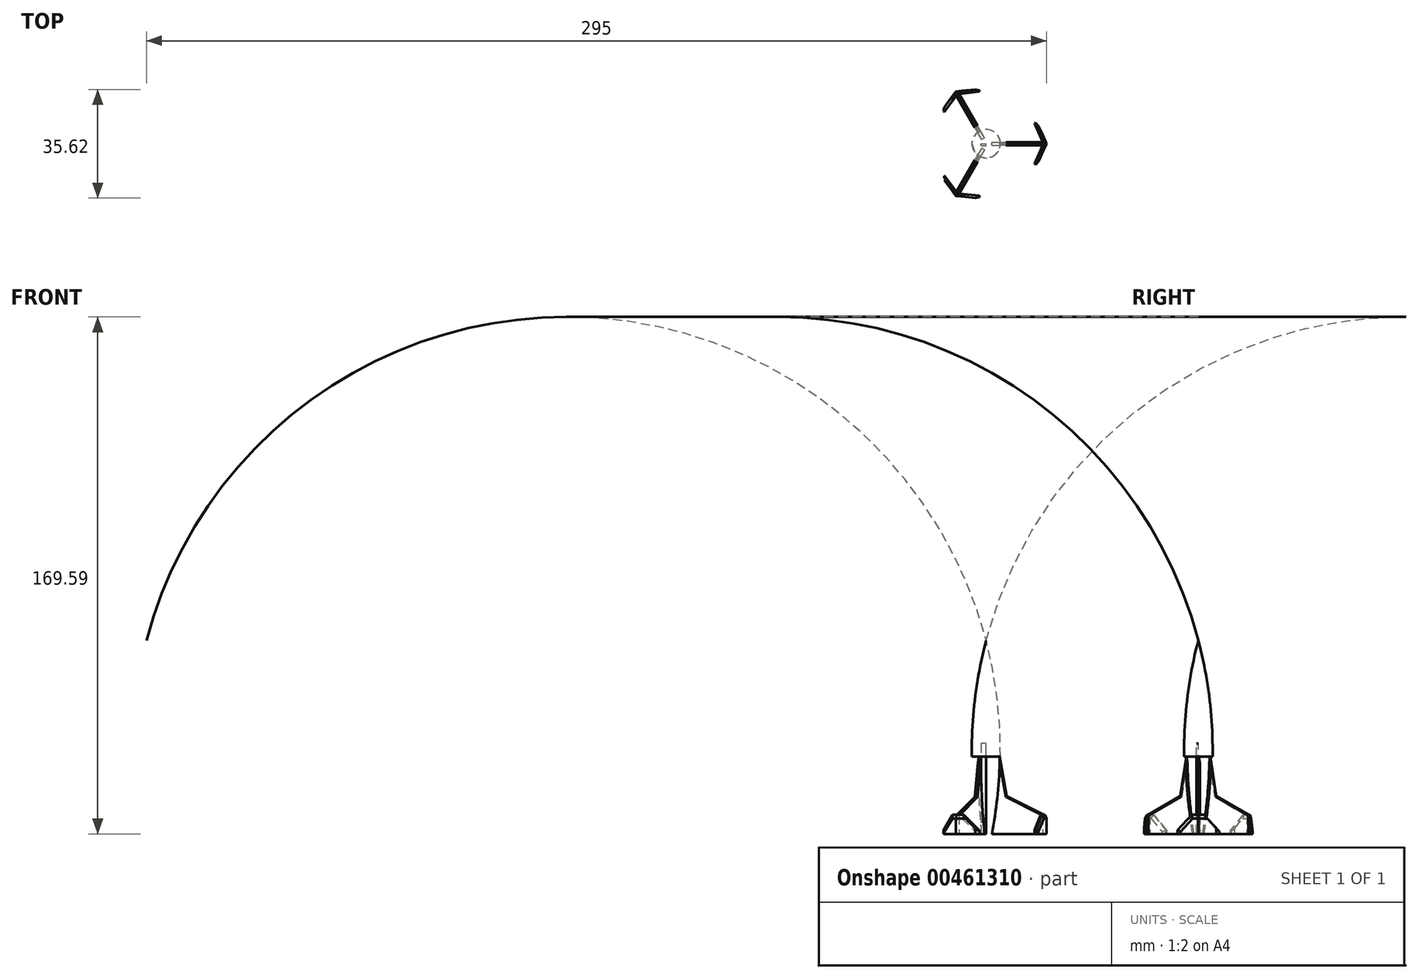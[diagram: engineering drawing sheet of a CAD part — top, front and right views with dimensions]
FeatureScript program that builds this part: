
annotation { "Feature Type Name" : "Feature", "Feature Type Description" : "" }
export const myFeature = defineFeature(function(context is Context, id is Id, definition is map)
    precondition{}
    {
        {
            var Q0;
            Q0=qCreatedBy(makeId("Front.planeOp"),FACE);
            var sketch = newSketch(context, id + "F0", { "sketchPlane" : qUnion([Q0])});
            skLineSegment(sketch, "E0", {"start": v(0, 0) * mm, "end": v(0, 63.5) * mm});
            skLineSegment(sketch, "E1", {"start": v(0, 0) * mm, "end": v(0, 25.4) * mm});
            skLineSegment(sketch, "E2", {"start": v(0, 25.4) * mm, "end": v(4.67, 25.4) * mm});
            skLineSegment(sketch, "E3", {"start": v(0, 0) * mm, "end": v(3.18, 0) * mm});
            skLineSegment(sketch, "E4", {"start": v(0, 0) * mm, "end": v(19.05, 0) * mm});
            skLineSegment(sketch, "E5", {"start": v(19.05, 0) * mm, "end": v(19.05, 6.35) * mm});
            skLineSegment(sketch, "E6", {"start": v(6.93, 12.46) * mm, "end": v(19.05, 6.35) * mm});
            skLineSegment(sketch, "E7", {"start": v(0, 0) * mm, "end": v(2.04, 0) * mm});
            skLineSegment(sketch, "E8", {"start": v(0, 0) * mm, "end": v(0, 19.05) * mm});
            skLineSegment(sketch, "E9", {"start": v(0, 19.05) * mm, "end": v(4.45, 19.05) * mm});
            skArc(sketch, "E10", {"start": v(2.04, 0) * mm, "mid": v(4.61, 31.87) * mm, "end": v(0, 63.5) * mm});
            skLineSegment(sketch, "E11", {"start": v(4.67, 25.4) * mm, "end": v(6.93, 12.46) * mm});
            skSolve(sketch);
        }
        {
            var Q0;
            {var subQ0=sQuery(id+"F0.wireOp",EDGE,"E0");Q0=makeQuery(id+"F0.imprint","IMPRINT",FACE,{"disambiguationData":[TD([[makeQuery(id+"F0.imprint","IMPRINT",EDGE,{"derivedFrom":subQ0}),-1.0]])]});}
            var Q1;
            {var subQ0=sQuery(id+"F0.wireOp",EDGE,"E1");Q1=makeQuery(id+"F0.imprint","IMPRINT",FACE,{"disambiguationData":[TD([[makeQuery(id+"F0.imprint","IMPRINT",EDGE,{"derivedFrom":subQ0}),-1.0]])]});}
            var Q2;
            Q2=makeQuery(id+"F0.imprint","IMPRINT",FACE,{"disambiguationData":[TD([[makeQuery(id+"F0.imprint","IMPRINT",EDGE,{"derivedFrom":sQuery(id+"F0.wireOp",EDGE,"E7")}),1.0]])]});
            var Q3;
            Q3=sQuery(id+"F0.wireOp",EDGE,"E8");
            revolve(context, id + "F1", {"entities" : qUnion([Q0, Q1, Q2]), "axis" : qUnion([Q3]), "revolveType" : RevolveType.FULL});
        }
        {
            var Q0;
            {var subQ4=sQuery(id+"F0.wireOp",EDGE,"E5");Q0=makeQuery(id+"F0.imprint","IMPRINT",FACE,{"disambiguationData":[TD([[makeQuery(id+"F0.imprint","IMPRINT",EDGE,{"derivedFrom":subQ4}),1.0]])]});}
            extrude(context, id + "F2", {"entities" : qUnion([Q0]), "depth" : 0.5 * mm, "hasSecondDirection" : true, "secondDirectionOppositeDirection" : true, "secondDirectionDepth" : 0.5 * mm});
        }
        {
            var Q0;
            Q0=qCreatedBy(makeId("Top.planeOp"),FACE);
            var sketch = newSketch(context, id + "F3", { "sketchPlane" : qUnion([Q0])});
            skLineSegment(sketch, "E12", {"start": v(18.99, 0) * mm, "end": v(16.06, 6.66) * mm});
            skLineSegment(sketch, "E13", {"start": v(16.06, 6.66) * mm, "end": v(16.86, 7.01) * mm});
            skLineSegment(sketch, "E14", {"start": v(16.86, 7.01) * mm, "end": v(19.94, 0) * mm});
            skLineSegment(sketch, "E15", {"start": v(19.94, 0) * mm, "end": v(18.99, 0) * mm});
            skSolve(sketch);
        }
        {
            var Q0;
            Q0 = qSketchRegion(id + "F3", true);
            extrude(context, id + "F4", {"entities" : qUnion([Q0]), "depth" : 6.35 * mm});
        }
        {
            var Q0;
            Q0=makeQuery(id+"F4.opExtrude","CAP_EDGE",EDGE,{"disambiguationData":[OSD([sQuery(id+"F3.wireOp",EDGE,"E13")])],"isStart":false});
            chamfer(context, id + "F5", {"entities" : qUnion([Q0]), "width" : 5.08 * mm, "tangentPropagation" : true});
        }
        {
            var Q0;
            Q0=makeQuery(id+"F4.opExtrude","SWEPT_BODY",BODY,{"disambiguationData":[OSD([sQuery(id+"F3.wireOp",EDGE,"E12"),sQuery(id+"F3.wireOp",EDGE,"E13"),sQuery(id+"F3.wireOp",EDGE,"E14"),sQuery(id+"F3.wireOp",EDGE,"E15")])]});
            var Q1;
            Q1=qCreatedBy(makeId("Front.planeOp"),FACE);
            mirror(context, id + "F6", {"operationType" : NewBodyOperationType.ADD, "entities" : qUnion([Q0]), "mirrorPlane" : qUnion([Q1])});
        }
        {
            var Q0;
            Q0=makeQuery(id+"F2.opExtrude","CAP_EDGE",EDGE,{"disambiguationData":[OSD([sQuery(id+"F0.wireOp",EDGE,"E11")])],"isStart":false});
            var Q1;
            Q1=makeQuery(id+"F2.opExtrude","CAP_EDGE",EDGE,{"disambiguationData":[OSD([sQuery(id+"F0.wireOp",EDGE,"E11")])],"isStart":true});
            var Q2;
            Q2=makeQuery(id+"F2.opExtrude","CAP_EDGE",EDGE,{"disambiguationData":[OSD([sQuery(id+"F0.wireOp",EDGE,"E6")])],"isStart":false});
            var Q3;
            Q3=makeQuery(id+"F2.opExtrude","CAP_EDGE",EDGE,{"disambiguationData":[OSD([sQuery(id+"F0.wireOp",EDGE,"E6")])],"isStart":true});
            chamfer(context, id + "F7", {"entities" : qUnion([Q0, Q1, Q2, Q3]), "width" : 0.38 * mm});
        }
        {
            var Q0;
            Q0=makeQuery(id+"F6.opPattern","COPY",EDGE,{"derivedFrom":makeQuery(id+"F4.opExtrude","CAP_EDGE",EDGE,{"disambiguationData":[OSD([sQuery(id+"F3.wireOp",EDGE,"E14")])],"isStart":false}),"instanceName":"1"});
            var Q1;
            Q1=makeQuery(id+"F4.opExtrude","CAP_EDGE",EDGE,{"disambiguationData":[OSD([sQuery(id+"F3.wireOp",EDGE,"E14")])],"isStart":false});
            var Q2;
            Q2=makeQuery(id+"F5.opChamfer","BLEND_EDGE",EDGE,{"blendedFrom":[makeQuery(id+"F4.opExtrude","CAP_EDGE",EDGE,{"disambiguationData":[OSD([sQuery(id+"F3.wireOp",EDGE,"E13")])],"isStart":false}),makeQuery(id+"F4.opExtrude","SWEPT_FACE",FACE,{"disambiguationData":[OSD([sQuery(id+"F3.wireOp",EDGE,"E14")])]})],"blendedInto":[makeQuery(id+"F4.opExtrude","SWEPT_FACE",FACE,{"disambiguationData":[OSD([sQuery(id+"F3.wireOp",EDGE,"E14")])]})]});
            var Q3;
            Q3=makeQuery(id+"F6.opPattern","COPY",EDGE,{"derivedFrom":makeQuery(id+"F5.opChamfer","BLEND_EDGE",EDGE,{"blendedFrom":[makeQuery(id+"F4.opExtrude","CAP_EDGE",EDGE,{"disambiguationData":[OSD([sQuery(id+"F3.wireOp",EDGE,"E13")])],"isStart":false}),makeQuery(id+"F4.opExtrude","SWEPT_FACE",FACE,{"disambiguationData":[OSD([sQuery(id+"F3.wireOp",EDGE,"E14")])]})],"blendedInto":[makeQuery(id+"F4.opExtrude","SWEPT_FACE",FACE,{"disambiguationData":[OSD([sQuery(id+"F3.wireOp",EDGE,"E14")])]})]}),"instanceName":"1"});
            var Q4;
            Q4=makeQuery(id+"F6.opPattern","COPY",EDGE,{"derivedFrom":makeQuery(id+"F4.opExtrude","SWEPT_EDGE",EDGE,{"disambiguationData":[OSD([sQuery(id+"F3.wireOp",EDGE,"E13"),sQuery(id+"F3.wireOp",EDGE,"E14")])]}),"instanceName":"1"});
            var Q5;
            Q5=makeQuery(id+"F4.opExtrude","SWEPT_EDGE",EDGE,{"disambiguationData":[OSD([sQuery(id+"F3.wireOp",EDGE,"E13"),sQuery(id+"F3.wireOp",EDGE,"E14")])]});
            chamfer(context, id + "F8", {"entities" : qUnion([Q0, Q1, Q2, Q3, Q4, Q5]), "chamferType" : ChamferType.OFFSET_ANGLE, "width" : 1.27 * mm, "oppositeDirection" : true, "angle" : 20 * degree, "tangentPropagation" : true});
        }
        {
            var Q0;
            Q0=qCreatedBy(makeId("Front.planeOp"),FACE);
            var sketch = newSketch(context, id + "F9", { "sketchPlane" : qUnion([Q0])});
            skLineSegment(sketch, "E16", {"start": v(0, 0) * mm, "end": v(0, 29.62) * mm});
            skLineSegment(sketch, "E17", {"start": v(0, 29.62) * mm, "end": v(-1.6, 29.62) * mm});
            skLineSegment(sketch, "E18", {"start": v(-1.6, 29.62) * mm, "end": v(-1.6, 0) * mm});
            skLineSegment(sketch, "E19", {"start": v(-1.6, 0) * mm, "end": v(0, 0) * mm});
            skSolve(sketch);
        }
        {
            var Q0;
            Q0 = qSketchRegion(id + "F9", true);
            extrude(context, id + "F10", {"entities" : qUnion([Q0]), "depth" : 0.64 * mm});
        }
        {
            var Q0;
            Q0=makeQuery(id+"F2.opExtrude","SWEPT_BODY",BODY,{"disambiguationData":[OSD([sQuery(id+"F0.wireOp",EDGE,"E4"),sQuery(id+"F0.wireOp",EDGE,"E5"),sQuery(id+"F0.wireOp",EDGE,"E6"),sQuery(id+"F0.wireOp",EDGE,"E10"),sQuery(id+"F0.wireOp",EDGE,"E11")])]});
            var Q1;
            Q1=makeQuery(id+"F4.opExtrude","SWEPT_BODY",BODY,{"disambiguationData":[OSD([sQuery(id+"F3.wireOp",EDGE,"E12"),sQuery(id+"F3.wireOp",EDGE,"E13"),sQuery(id+"F3.wireOp",EDGE,"E14"),sQuery(id+"F3.wireOp",EDGE,"E15")])]});
            transform(context, id + "F11", {"entities" : qUnion([Q0, Q1]), "transformType" : TransformType.TRANSLATION_3D, "dx" : -0.18 * mm, "dy" : 0 * mm, "dz" : 0 * mm, "makeCopy" : false});
        }
        {
            var Q0;
            Q0=makeQuery(id+"F2.opExtrude","SWEPT_BODY",BODY,{"disambiguationData":[OSD([sQuery(id+"F0.wireOp",EDGE,"E4"),sQuery(id+"F0.wireOp",EDGE,"E5"),sQuery(id+"F0.wireOp",EDGE,"E6"),sQuery(id+"F0.wireOp",EDGE,"E10"),sQuery(id+"F0.wireOp",EDGE,"E11")])]});
            var Q1;
            Q1=makeQuery(id+"F4.opExtrude","SWEPT_BODY",BODY,{"disambiguationData":[OSD([sQuery(id+"F3.wireOp",EDGE,"E12"),sQuery(id+"F3.wireOp",EDGE,"E13"),sQuery(id+"F3.wireOp",EDGE,"E14"),sQuery(id+"F3.wireOp",EDGE,"E15")])]});
            var Q2;
            Q2=sQuery(id+"F0.wireOp",EDGE,"E8");
            circularPattern(context, id + "F12", {"operationType" : NewBodyOperationType.ADD, "entities" : qUnion([Q0, Q1]), "axis" : qUnion([Q2]), "angle" : 360 * degree, "instanceCount" : 3, "equalSpace" : true});
        }
    });
